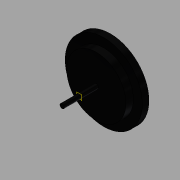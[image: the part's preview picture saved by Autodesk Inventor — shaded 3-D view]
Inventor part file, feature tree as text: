
AUTODESK INVENTOR PART (.ipt)
format: ipt  version: 2015 (Build 190159000, 159)  size: 150,016 bytes
history: native  units: in
note: dims shown in document units (in); Inventor stores cm internally (conversion verified against a paired STEP export)
features: sketch x5, other x3, extrude x2, fillet x2, plane x1
ambient origin geometry x8: Origin, YZ Plane, XZ Plane, XY Plane, X Axis, Y Axis, Z Axis, Center Point
bodies: Solid1 (feature_tree)
feature tree (13):
  other  "rueda_MIR3.ipt"
  extrude  "Extrusion1"  Depth=0.1969in TaperAngle=0.0deg
  extrude  "Extrusion2"  Depth=0.0787in TaperAngle=0.0deg
  fillet  "Fillet1"  Radius=0.0787in
  fillet  "Fillet2"  Radius=0.0787in
  other  "Solid1::rueda_MIR3.ipt"
  other  "TaggingFeature1"
  sketch  "Sketch2"  dims[d0=0.3937in d2=0.1969in d3=0.0in]
  sketch  "Sketch3"  dims[d4=0.0787in d5=0.0787in d6=0.0in d7=0.0787in d8=0.0787in]
  sketch  "Sketch7"
  plane  "Work Plane1"
  sketch  "Sketch5"
  sketch  "Sketch6"
